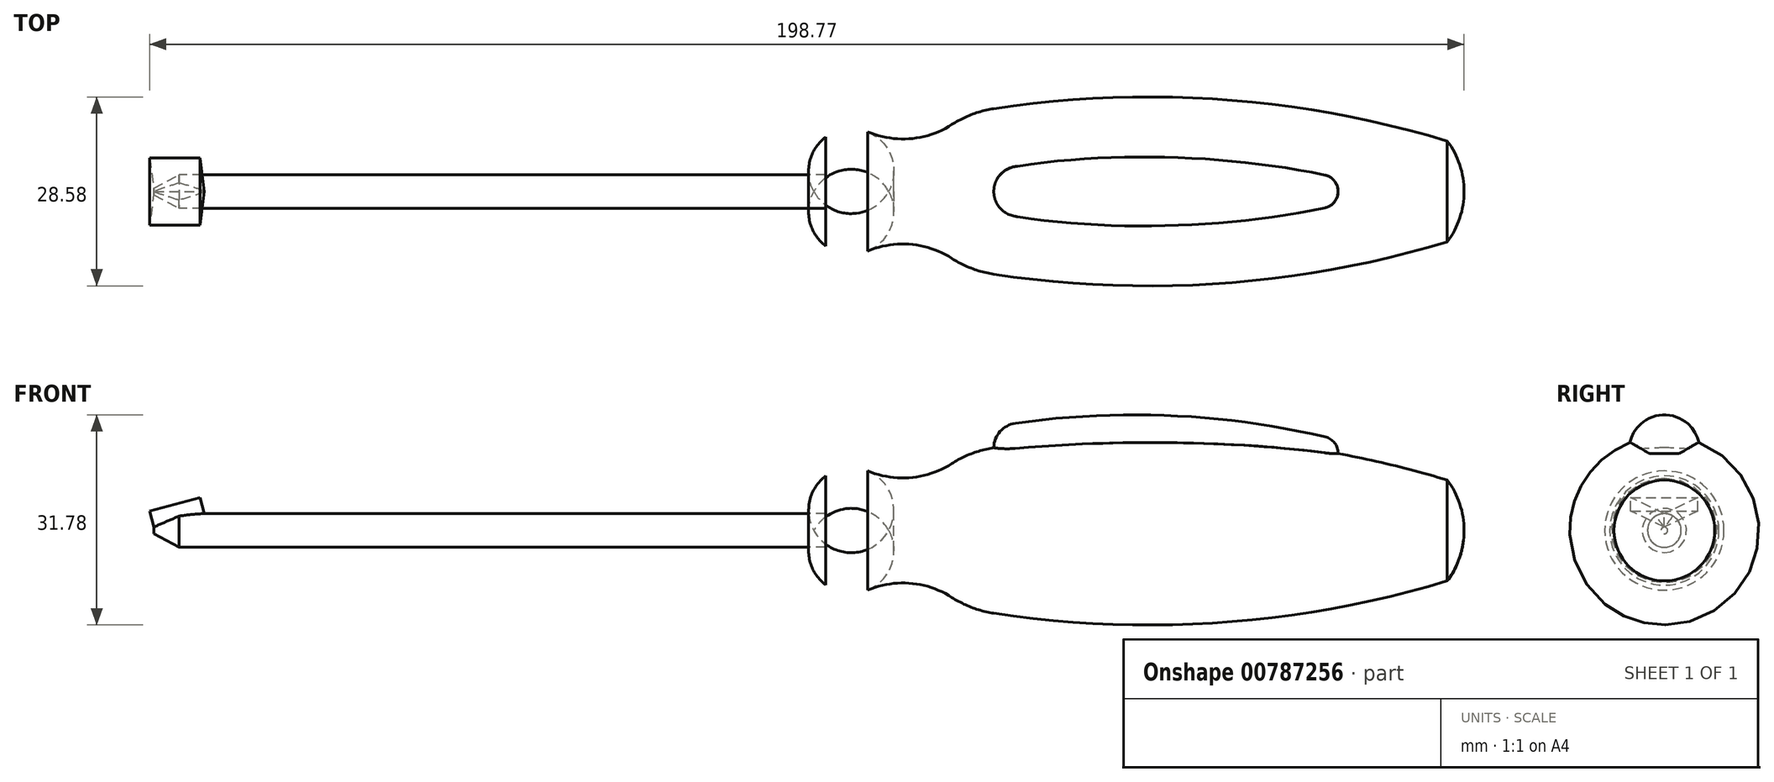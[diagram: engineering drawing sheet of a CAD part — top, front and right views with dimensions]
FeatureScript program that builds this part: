
annotation { "Feature Type Name" : "Feature", "Feature Type Description" : "" }
export const myFeature = defineFeature(function(context is Context, id is Id, definition is map)
    precondition{}
    {
        {
            var Q0;
            Q0=qCreatedBy(makeId("Front.planeOp"),FACE);
            var sketch = newSketch(context, id + "F0", { "sketchPlane" : qUnion([Q0])});
            skLineSegment(sketch, "E0", {"start": v(-101.6, 0) * mm, "end": v(96.52, 0) * mm});
            skLineSegment(sketch, "E1", {"start": v(96.52, 0) * mm, "end": v(117.55, 0) * mm, "construction": true});
            skLineSegment(sketch, "E2", {"start": v(50.8, 2.54) * mm, "end": v(-97.8, 2.54) * mm});
            skLineSegment(sketch, "E3", {"start": v(-101.6, 0.5) * mm, "end": v(-101.6, 0) * mm});
            skLineSegment(sketch, "E4", {"start": v(0, 2.54) * mm, "end": v(0, 8.25) * mm});
            skArc(sketch, "E5", {"start": v(6.35, 9.02) * mm, "mid": v(3.07, 9.48) * mm, "end": v(0, 8.25) * mm});
            skArc(sketch, "E6", {"start": v(6.35, 9.02) * mm, "mid": v(12.84, 7.99) * mm, "end": v(19.05, 10.11) * mm});
            skArc(sketch, "E7", {"start": v(25.4, 12.52) * mm, "mid": v(22.1, 11.65) * mm, "end": v(19.05, 10.11) * mm});
            skArc(sketch, "E8", {"start": v(93.98, 7.62) * mm, "mid": v(59.96, 13.9) * mm, "end": v(25.4, 12.52) * mm});
            skArc(sketch, "E9", {"start": v(96.52, 0) * mm, "mid": v(95.87, 4.02) * mm, "end": v(93.98, 7.62) * mm});
            skArc(sketch, "E10.0", {"start": v(25.17, 14.02) * mm, "mid": v(22.01, 13.24) * mm, "end": v(19.05, 11.9) * mm});
            skArc(sketch, "E10.1", {"start": v(92.95, 9.52) * mm, "mid": v(59.3, 15.46) * mm, "end": v(25.17, 14.02) * mm});
            skLineSegment(sketch, "E11", {"start": v(19.05, 11.9) * mm, "end": v(19.05, 10.11) * mm});
            skArc(sketch, "E12", {"start": v(93.98, 7.62) * mm, "mid": v(93.86, 8.78) * mm, "end": v(92.95, 9.52) * mm});
            skPoint(sketch, "E13.orphan", {"position": v(0, 0) * mm});
            skLineSegment(sketch, "E14", {"start": v(50.8, 2.54) * mm, "end": v(50.8, 0) * mm});
            skLineSegment(sketch, "E15", {"start": v(-101.6, 0.5) * mm, "end": v(-97.8, 2.54) * mm});
            skPoint(sketch, "E16.orphan", {"position": v(-101.6, 2.54) * mm});
            skSolve(sketch);
        }
        {
            var Q0;
            Q0=qCreatedBy(makeId("Front.planeOp"),FACE);
            var sketch = newSketch(context, id + "F1", { "sketchPlane" : qUnion([Q0])});
            skLineSegment(sketch, "E17", {"start": v(25.4, 12.52) * mm, "end": v(77.47, 11.64) * mm});
            skArc(sketch, "E18", {"start": v(28.67, 16.22) * mm, "mid": v(26.35, 14.97) * mm, "end": v(25.4, 12.52) * mm});
            skArc(sketch, "E19", {"start": v(77.47, 11.64) * mm, "mid": v(76.93, 13.25) * mm, "end": v(75.5, 14.16) * mm});
            skArc(sketch, "E20", {"start": v(75.5, 14.16) * mm, "mid": v(52.19, 17.37) * mm, "end": v(28.67, 16.22) * mm});
            skSolve(sketch);
        }
        {
            var Q0;
            Q0=qCreatedBy(makeId("Front.planeOp"),FACE);
            var sketch = newSketch(context, id + "F2", { "sketchPlane" : qUnion([Q0])});
            skLineSegment(sketch, "E21", {"start": v(-101.6, 0.5) * mm, "end": v(-93.98, 2.54) * mm});
            skSolve(sketch);
        }
        {
            var Q0;
            Q0=sQuery(id+"F2.wireOp",VERTEX,"E21.start");
            var Q1;
            Q1=sQuery(id+"F2.wireOp",EDGE,"E21");
            cPlane(context, id + "F3", {"entities" : qUnion([Q0, Q1]), "cplaneType" : CPlaneType.LINE_POINT, "offset" : 25.4 * mm, "width" : 152.4 * mm, "height" : 152.4 * mm});
        }
        {
            var Q0;
            Q0=qCreatedBy(id+"F3.planeOp",FACE);
            var sketch = newSketch(context, id + "F4", { "sketchPlane" : qUnion([Q0])});
            skLineSegment(sketch, "E22", {"start": v(5.08, 29.2) * mm, "end": v(0, 26.67) * mm});
            skLineSegment(sketch, "E23", {"start": v(0, 26.67) * mm, "end": v(-5.08, 29.2) * mm});
            skLineSegment(sketch, "E24", {"start": v(-5.08, 29.2) * mm, "end": v(5.08, 29.2) * mm});
            skLineSegment(sketch, "E25", {"start": v(0, 29.2) * mm, "end": v(0, 26.67) * mm, "construction": true});
            skSolve(sketch);
        }
        {
            var Q0;
            {var subQ0=sQuery(id+"F0.wireOp",EDGE,"E4");Q0=makeQuery(id+"F0.imprint","IMPRINT",FACE,{"disambiguationData":[TD([[makeQuery(id+"F0.imprint","IMPRINT",EDGE,{"derivedFrom":subQ0}),-1.0]])]});}
            var Q1;
            Q1=sQuery(id+"F0.wireOp",EDGE,"E1");
            revolve(context, id + "F5", {"surfaceOperationType" : NewSurfaceOperationType.NEW, "entities" : qUnion([Q0]), "axis" : qUnion([Q1]), "revolveType" : RevolveType.FULL});
        }
        {
            var Q0;
            Q0=makeQuery(id+"F1.imprint","IMPRINT",FACE,{"disambiguationData":[TD([[makeQuery(id+"F1.imprint","IMPRINT",EDGE,{"derivedFrom":sQuery(id+"F1.wireOp",EDGE,"E17")}),1.0]])]});
            var Q1;
            Q1=sQuery(id+"F1.wireOp",EDGE,"E17");
            revolve(context, id + "F6", {"operationType" : NewBodyOperationType.ADD, "surfaceOperationType" : NewSurfaceOperationType.NEW, "entities" : qUnion([Q0]), "axis" : qUnion([Q1]), "revolveType" : RevolveType.FULL});
        }
        {
            var Q0;
            {var subQ0=sQuery(id+"F0.wireOp",EDGE,"E3");Q0=makeQuery(id+"F0.imprint","IMPRINT",FACE,{"disambiguationData":[TD([[makeQuery(id+"F0.imprint","IMPRINT",EDGE,{"derivedFrom":subQ0}),1.0]])]});}
            var Q1;
            Q1=sQuery(id+"F0.wireOp",EDGE,"E1");
            revolve(context, id + "F7", {"operationType" : NewBodyOperationType.ADD, "surfaceOperationType" : NewSurfaceOperationType.NEW, "entities" : qUnion([Q0]), "axis" : qUnion([Q1]), "revolveType" : RevolveType.FULL});
        }
        {
            var Q0;
            Q0=makeQuery(id+"F4.imprint","IMPRINT",FACE,{"disambiguationData":[TD([[makeQuery(id+"F4.imprint","IMPRINT",EDGE,{"derivedFrom":sQuery(id+"F4.wireOp",EDGE,"E22")}),-1.0]])]});
            var Q1;
            Q1=sQuery(id+"F2.wireOp",EDGE,"E21");
            sweep(context, id + "F8", {"operationType" : NewBodyOperationType.REMOVE, "profiles" : qUnion([Q0]), "path" : qUnion([Q1])});
        }
        {
            var Q0;
            Q0=makeQuery(id+"F4.imprint","IMPRINT",FACE,{"disambiguationData":[TD([[makeQuery(id+"F4.imprint","IMPRINT",EDGE,{"derivedFrom":sQuery(id+"F4.wireOp",EDGE,"E22")}),-1.0]])]});
            var Q1;
            Q1=qConstructionFilter(qBodyType(qCreatedBy(id+"F2",EDGE),BodyType.WIRE),ConstructionObject.NO);
            sweep(context, id + "F9", {"profiles" : qUnion([Q0]), "path" : qUnion([Q1])});
        }
    });
